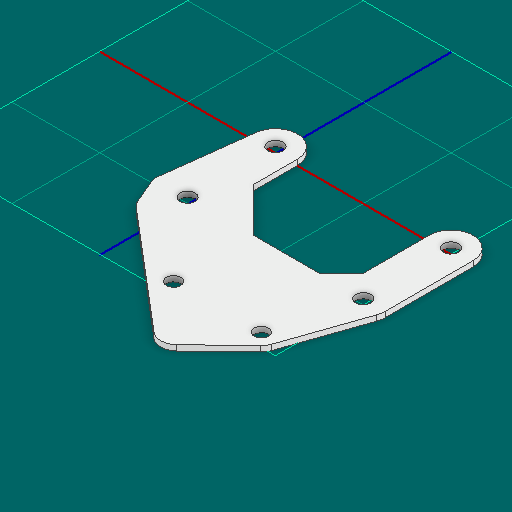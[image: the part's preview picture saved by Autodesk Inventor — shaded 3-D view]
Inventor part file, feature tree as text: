
AUTODESK INVENTOR PART (.ipt)
format: ipt  version: 2025 (Build 290162000, 162)  size: 147,456 bytes
history: native  units: in
note: dims shown in document units (in); Inventor stores cm internally (conversion verified against a paired STEP export)
features: other x3, extrude x1, sketch x1
ambient origin geometry x8: Origin, YZ Plane, XZ Plane, XY Plane, X Axis, Y Axis, Z Axis, Center Point
bodies: Solid1 (feature_tree)
feature tree (5):
  other  "Blocks"
  extrude  "Extrusion1"  Depth=0.25in
  sketch  "Sketch1"  dims[d0=0.164in d1=0.375in d2=0.5in d3=0.5in d4=0.25in d5=0.25in d6=0.164in d7=0.1875in d9=0.125in d10=0.0625in d11=0.0in d12=1.911in d14=0.125in d16=1.0in d17=1.9106in d18=0.25in]
  other  "main"
  other  "main:1"
